# Revit family: BE_84126_de_DE
name_source: partatom
category: Leuchten
revit_build: Autodesk Revit 2015 (Build: 20160512_0715(x64)
units: mm (PartAtom-declared; Revit-internal decimal feet)

## types (4) — shared parameters
AC/DC = AC/DC
Aktualisierung = 2017-09-01T04:09:39
BEGA_Dummy = Nein
BEGA_IES = Ja
BEGA_Intern = Ja
BEGA_Intern_Konstruktion = Ja
BEGA_Intern_an = Ja
BEGA_Intern_aus = Ja
Befestigungsabstand = 240 x 240 mm
Befestigungsbohrung = Ø 18 mm
Beschreibung = Lichtbauelement
Beschreibung_Sonderanfertigung = Hier können Sie Informationen zur Sonderanfertigung eintragen.
CE_Konformität = ja
Energieeffizienzklasse = LED A++ - A
Farbwiedergabeindex = Ra > 80
Frequenz = 0/50-60 Hz
Gewicht = 38.0 kg
Hersteller = BEGA
Lampe = LED 39.2 W
Lastklassifizierung = Beleuchtung
Lebensdauerkriterien = L70B50 @ 25 °C = 500000 h
Logo = BEGA_Logo.png
M_W = Nein
Material_02 = BEGA_Oberfläche_Silber_matt
Material_03 = BEGA_Oberfläche_Weiss_matt
Material_06 = BEGA_Oberfläche_Edelstahl_gebürstet
Material_08 = BEGA_Oberfläche_Stahl_verzinkt
Material_09 = BEGA_Glas_klar
Material_11 = BEGA_Glas_opal
Material_15 = BEGA_Leuchtmedium_matt
Material_17 = BEGA_Reflektor
Material_18 = BEGA_Gummi_schwarz
Produktdatenblatt = http://www.bega.de
Scheinlast = 0 VA
Schutzart = IP 65
Schutzklasse = I
Sonderanfertigung = Nein
Spannung = 240 V
Typenbild = 84126.png
URL = http://www.bega.de
Umgebungstemperatur = 25 °C
Windangriffsfläche = 0.89 m²
zero-valued in all types: Vorgabe-Ansicht

## per-type parameters (varying)
| type | BEGA_IES1 | BEGA_IES2 | Bestellnummer | Farbtemperatur | LED_Modulbezeichnung | Lampenlichtstrom | Leuchtenlichtstrom | M_A | M_G | Modell |
| BEGA_84126_Grafit_K4 | Nein | Ja | 84126 | 4000 K | 4x LED-0147/840 | 7300 lm | 4781 lm | Nein | Ja | 84126 |
| BEGA_84126_Silber_K4 | Nein | Ja | 84126A | 4000 K | 4x LED-0147/840 | 7300 lm | 4781 lm | Ja | Nein | 84126A |
| BEGA_84126_Silber_K3 | Ja | Nein | 84126AK3 | 3000 K | 4x LED-0147/830 | 7140 lm | 4670 lm | Ja | Nein | 84126AK3 |
| BEGA_84126_Grafit_K3 | Ja | Nein | 84126K3 | 3000 K | 4x LED-0147/830 | 7140 lm | 4670 lm | Nein | Ja | 84126K3 |

## geometry (parser evidence)
native form markers: Sweep x13
no freeform markers — native parametric forms only
